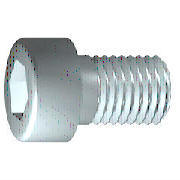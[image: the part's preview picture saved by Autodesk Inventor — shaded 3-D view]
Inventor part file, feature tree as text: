
AUTODESK INVENTOR PART (.ipt)
format: ipt  version: 2020 (Build 240168000, 168)  size: 193,536 bytes
history: native  units: mm (DEFAULTED — no unit token found)
features: sketch x2, extrude x1, plane x1, fillet x1
ambient origin geometry x7: Origin, YZ Plane, XY Plane, X Axis, Y Axis, Z Axis, Center Point
bodies: Solid1 (feature_tree), Body (feature_tree)
feature tree (5):
  extrude  "Slot"  Depth=2.8mm
  plane  "Work Plane1"
  fillet  "Fillet2"  Radius=2.8mm
  sketch  "Sketch1"  dims[d1=17.9mm d2=0.429515mm d3=2.8mm]
  sketch  "Sketch2"  dims[d4=2.3mm d5=60.0deg d6=4.0mm d7=4.0mm d8=2.886751mm d9=7.0mm d10=90.0deg d11=10.0mm d12=0.0mm d13=17.9mm d14=0.0mm d15=0.429415mm d16=0.429415mm d17=0.4mm d19=0.0mm d26=20.0mm d27=45.0deg d28=0.0mm d29=0.0mm d30=0.1mm]
